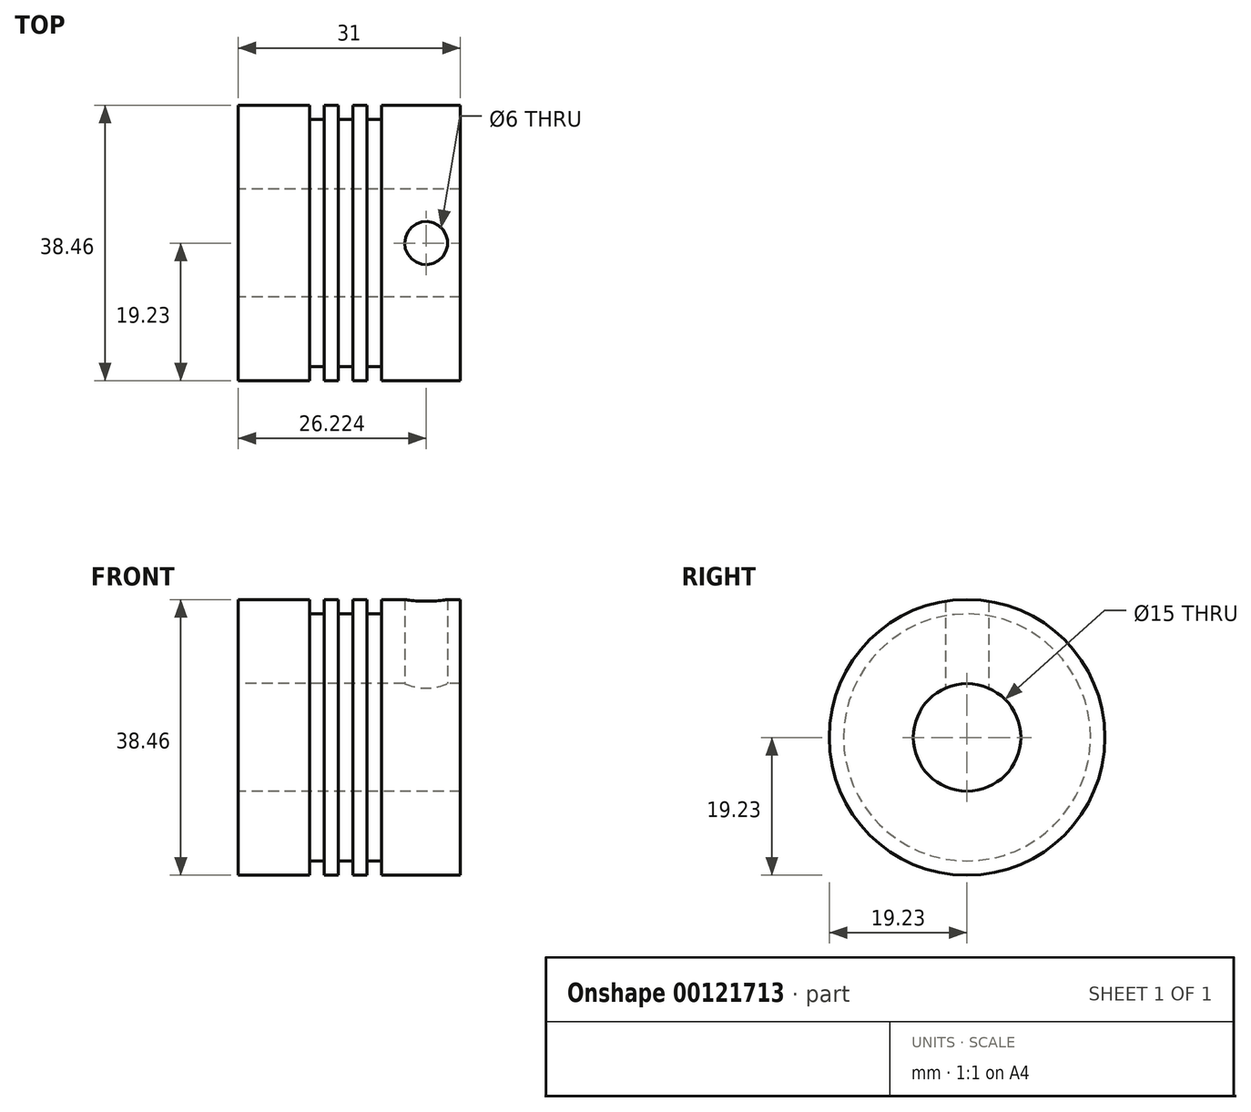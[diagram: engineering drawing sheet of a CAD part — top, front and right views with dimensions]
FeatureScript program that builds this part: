
annotation { "Feature Type Name" : "Feature", "Feature Type Description" : "" }
export const myFeature = defineFeature(function(context is Context, id is Id, definition is map)
    precondition{}
    {
        {
            var Q0;
            Q0=qCreatedBy(makeId("Front.planeOp"),FACE);
            var sketch = newSketch(context, id + "F0", { "sketchPlane" : qUnion([Q0])});
            skLineSegment(sketch, "E0", {"start": v(0, 0) * mm, "end": v(-78.33, 0) * mm});
            skLineSegment(sketch, "E1", {"start": v(-78.33, 0) * mm, "end": v(-78.33, 19.23) * mm});
            skLineSegment(sketch, "E2", {"start": v(-78.33, 19.23) * mm, "end": v(-68.33, 19.23) * mm});
            skLineSegment(sketch, "E3", {"start": v(-68.33, 19.23) * mm, "end": v(-68.33, 17.23) * mm});
            skLineSegment(sketch, "E4", {"start": v(-68.33, 17.23) * mm, "end": v(-66.33, 17.23) * mm});
            skLineSegment(sketch, "E5", {"start": v(-66.33, 17.23) * mm, "end": v(-66.33, 19.23) * mm});
            skLineSegment(sketch, "E6", {"start": v(-66.33, 19.23) * mm, "end": v(-64.33, 19.23) * mm});
            skLineSegment(sketch, "E7", {"start": v(-64.33, 19.23) * mm, "end": v(-64.33, 17.23) * mm});
            skLineSegment(sketch, "E8", {"start": v(-64.33, 17.23) * mm, "end": v(-62.33, 17.23) * mm});
            skLineSegment(sketch, "E9", {"start": v(-62.33, 17.23) * mm, "end": v(-62.33, 19.23) * mm});
            skLineSegment(sketch, "E10", {"start": v(-47.33, 19.23) * mm, "end": v(-47.33, 0) * mm});
            skLineSegment(sketch, "E11", {"start": v(-62.33, 19.23) * mm, "end": v(-60.33, 19.23) * mm});
            skLineSegment(sketch, "E12", {"start": v(-60.33, 19.23) * mm, "end": v(-60.33, 17.23) * mm});
            skLineSegment(sketch, "E13", {"start": v(-60.33, 17.23) * mm, "end": v(-58.33, 17.23) * mm});
            skLineSegment(sketch, "E14", {"start": v(-58.33, 17.23) * mm, "end": v(-58.33, 19.23) * mm});
            skLineSegment(sketch, "E15", {"start": v(-58.33, 19.23) * mm, "end": v(-47.33, 19.23) * mm});
            skSolve(sketch);
        }
        {
            var Q0;
            {var subQ0=sQuery(id+"F0.wireOp",EDGE,"E1");Q0=makeQuery(id+"F0.imprint","IMPRINT",FACE,{"disambiguationData":[TD([[makeQuery(id+"F0.imprint","IMPRINT",EDGE,{"derivedFrom":subQ0}),-1.0]])]});}
            var Q1;
            Q1=sQuery(id+"F0.wireOp",EDGE,"E0");
            revolve(context, id + "F1", {"entities" : qUnion([Q0]), "axis" : qUnion([Q1]), "revolveType" : RevolveType.FULL});
        }
        {
            var Q0;
            Q0=makeQuery(id+"F1.opRevolve","SWEPT_FACE",FACE,{"disambiguationData":[OSD([sQuery(id+"F0.wireOp",EDGE,"E1")])]});
            var sketch = newSketch(context, id + "F2", { "sketchPlane" : qUnion([Q0])});
            skCircle(sketch, "E16", {"center": v(0, 0) * mm, "radius": 7.5 * mm});
            skSolve(sketch);
        }
        {
            var Q0;
            Q0 = qSketchRegion(id + "F2", true);
            extrude(context, id + "F3", {"entities" : qUnion([Q0]), "operationType" : NewBodyOperationType.REMOVE, "oppositeDirection" : true, "depth" : 40 * mm});
        }
        {
            var Q0;
            Q0=qCreatedBy(makeId("Top.planeOp"),FACE);
            var sketch = newSketch(context, id + "F4", { "sketchPlane" : qUnion([Q0])});
            skCircle(sketch, "E17", {"center": v(-52.1, 0) * mm, "radius": 3 * mm});
            skSolve(sketch);
        }
        {
            var Q0;
            Q0 = qSketchRegion(id + "F4", true);
            extrude(context, id + "F5", {"entities" : qUnion([Q0]), "operationType" : NewBodyOperationType.REMOVE, "depth" : 25 * mm});
        }
    });
